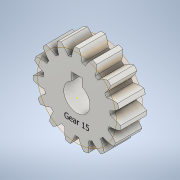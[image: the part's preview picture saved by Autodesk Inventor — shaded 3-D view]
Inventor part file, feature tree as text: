
AUTODESK INVENTOR PART (.ipt)
format: ipt  version: 2021 (Build 250183000, 183)  size: 236,032 bytes
history: native  units: mm (DEFAULTED — no unit token found)
features: sketch x4, plane x3, other x3, extrude x2
ambient origin geometry x8: Origin, YZ Plane, XZ Plane, XY Plane, X Axis, Y Axis, Z Axis, Center Point
bodies: Solid1 (feature_tree)
feature tree (12):
  extrude  "Extrusion1"  Depth=5.0mm TaperAngle=0.0deg
  plane  "Work Plane2"
  plane  "Work Plane8"
  plane  "Work Plane9"
  other  "Spur Gear"
  extrude  "Extrusion2"  Depth=10.0mm TaperAngle=0.0deg
  sketch  "Sketch5"  dims[d17=0.0mm d34=2.094395mm d39=0.0mm d41=0.0mm d43=22.5mm d46=22.5mm d47=0.0mm d48=0.0mm d57=5.0mm d58=2.0mm d59=1.5mm d60=5.0mm d61=0.0mm d62=0.5mm d63=0.872665mm]
  sketch  "Sketch1"  dims[d0=16.6mm d1=5.0mm d2=0.0mm]
  sketch  "Sketch2"  dims[d3=15.0mm d4=10.0mm d5=0.0mm]
  other  "Srf1"
  sketch  "Sketch4"  dims[d16=22.5mm]
  other  "Pitch Diameter"
